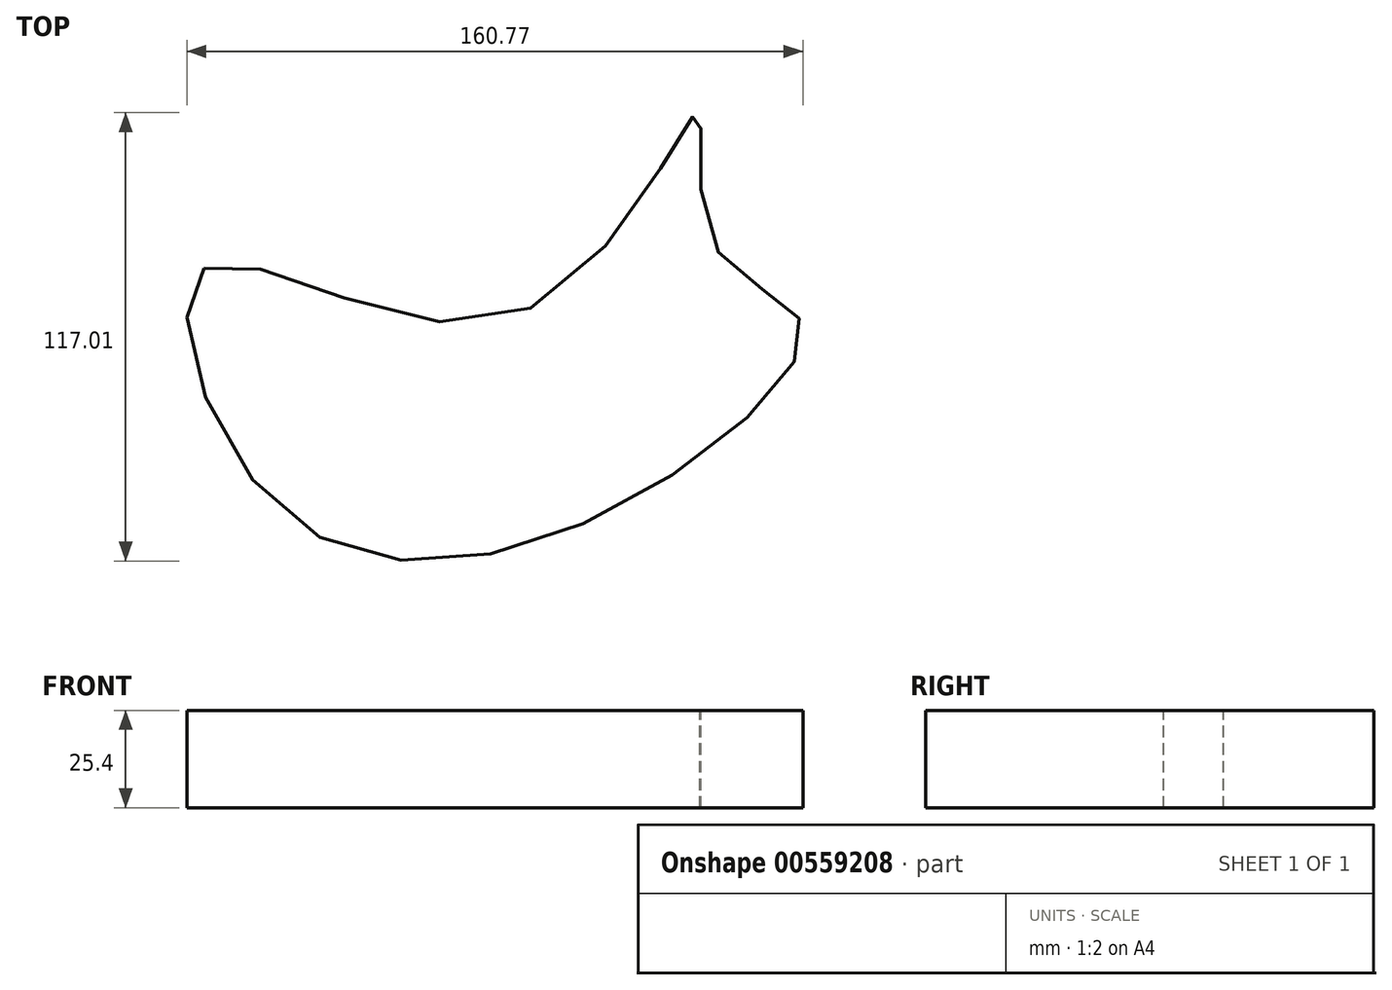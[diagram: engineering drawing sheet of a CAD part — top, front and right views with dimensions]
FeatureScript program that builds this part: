
annotation { "Feature Type Name" : "Feature", "Feature Type Description" : "" }
export const myFeature = defineFeature(function(context is Context, id is Id, definition is map)
    precondition{}
    {
        {
            var Q0;
            Q0=qCreatedBy(makeId("Top.planeOp"),FACE);
            var sketch = newSketch(context, id + "F0", { "sketchPlane" : qUnion([Q0])});
            skFitSpline(sketch, "E0", {"points": [v(-215.49, -124.41) * mm, v(-134.64, -136.73) * mm, v(-86.52, -83.82) * mm, v(-82.8, -117.72) * mm, v(-59.46, -139.2) * mm, v(-108.71, -187.3) * mm, v(-196.5, -186.64) * mm, v(-215.49, -124.41) * mm]});
            skSolve(sketch);
        }
        {
            var Q0;
            Q0=sQuery(id+"F0.wireOp",EDGE,"E0");
            extrude(context, id + "F1", {"bodyType" : ToolBodyType.SURFACE, "surfaceEntities" : qUnion([Q0]), "depth" : 25.4 * mm, "offsetDistance" : 25.4 * mm});
        }
    });
